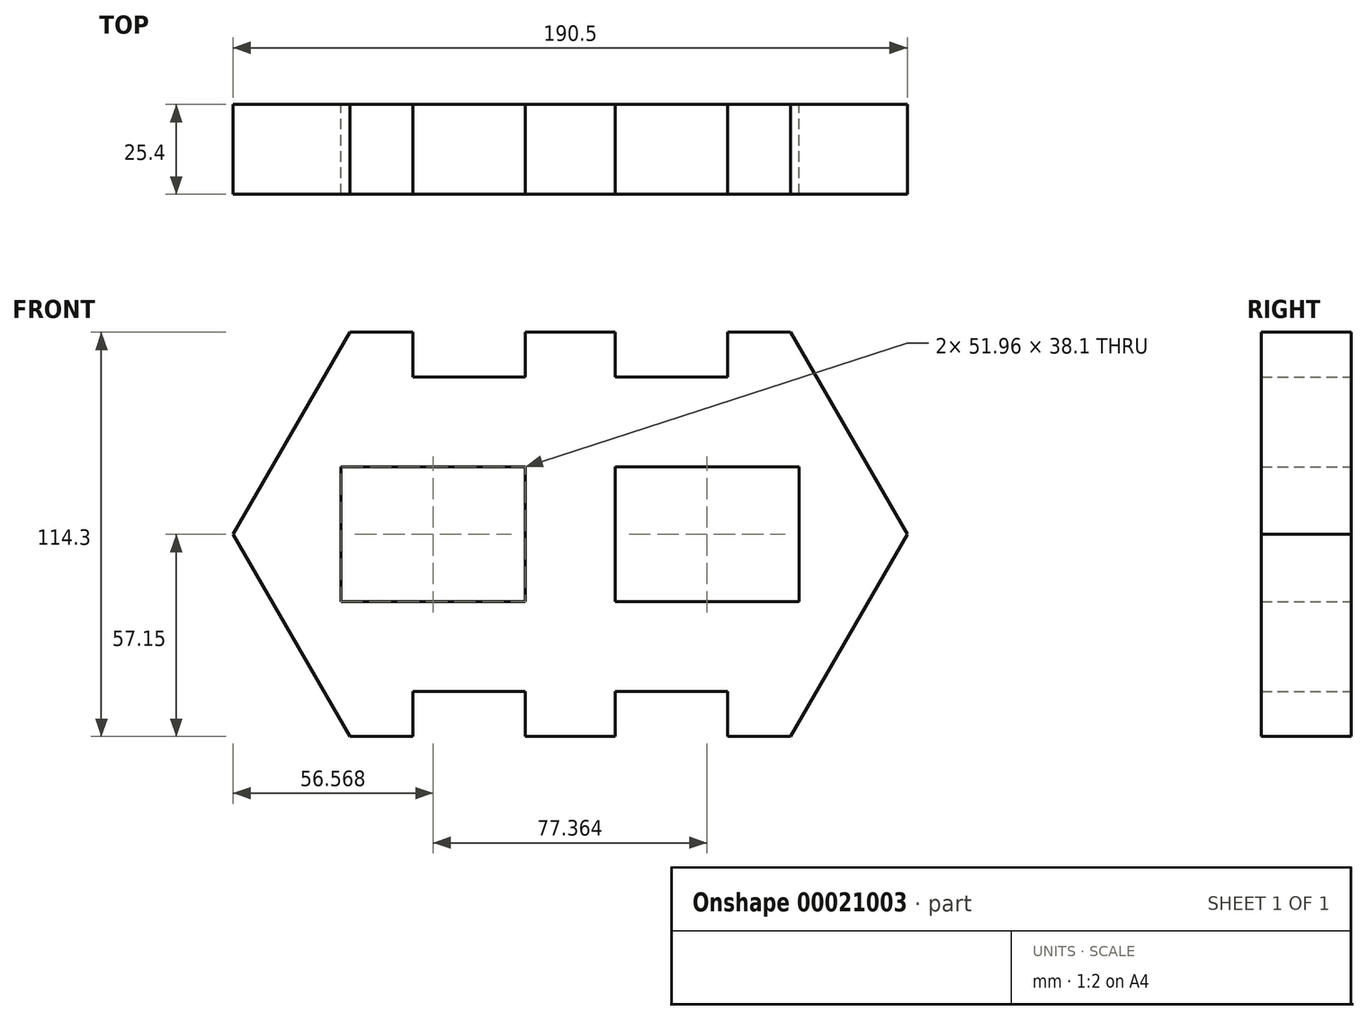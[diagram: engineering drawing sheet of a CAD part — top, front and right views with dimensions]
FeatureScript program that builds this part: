
annotation { "Feature Type Name" : "Feature", "Feature Type Description" : "" }
export const myFeature = defineFeature(function(context is Context, id is Id, definition is map)
    precondition{}
    {
        {
            var Q0;
            Q0=qCreatedBy(makeId("Front.planeOp"),FACE);
            var sketch = newSketch(context, id + "F0", { "sketchPlane" : qUnion([Q0])});
            skLineSegment(sketch, "E0.rect.bottom", {"start": v(-62.25, 57.15) * mm, "end": v(-44.45, 57.15) * mm});
            skLineSegment(sketch, "E0.rect.top", {"start": v(-62.25, -57.15) * mm, "end": v(-44.45, -57.15) * mm});
            skPoint(sketch, "E0.rect.middle", {"position": v(0, 0) * mm});
            skLineSegment(sketch, "E1.rect.bottom", {"start": v(-12.7, 57.15) * mm, "end": v(12.7, 57.15) * mm});
            skLineSegment(sketch, "E1.rect.top", {"start": v(-12.7, -57.15) * mm, "end": v(12.7, -57.15) * mm});
            skLineSegment(sketch, "E1.rect.left", {"start": v(-12.7, 57.15) * mm, "end": v(-12.7, 44.45) * mm});
            skLineSegment(sketch, "E1.rect.right", {"start": v(12.7, 57.15) * mm, "end": v(12.7, 44.45) * mm});
            skPoint(sketch, "E2", {"position": v(12.7, 44.45) * mm});
            skPoint(sketch, "E3", {"position": v(44.45, 57.15) * mm});
            skLineSegment(sketch, "E4", {"start": v(44.45, 57.15) * mm, "end": v(44.45, 44.45) * mm});
            skLineSegment(sketch, "E5", {"start": v(12.7, 44.45) * mm, "end": v(44.45, 44.45) * mm});
            skLineSegment(sketch, "E6", {"start": v(44.45, 44.45) * mm, "end": v(44.45, 57.15) * mm});
            skLineSegment(sketch, "E7.trimOffspring", {"start": v(44.45, 57.15) * mm, "end": v(62.25, 57.15) * mm});
            skPoint(sketch, "E8", {"position": v(64.66, 19.05) * mm});
            skLineSegment(sketch, "E9.bottom", {"start": v(64.66, 19.05) * mm, "end": v(12.7, 19.05) * mm});
            skLineSegment(sketch, "E9.top", {"start": v(64.66, -19.05) * mm, "end": v(12.7, -19.05) * mm});
            skLineSegment(sketch, "E10", {"start": v(95.25, 0) * mm, "end": v(62.25, 57.15) * mm});
            skLineSegment(sketch, "E11", {"start": v(95.25, 0) * mm, "end": v(62.25, -57.15) * mm});
            skLineSegment(sketch, "E12.bottom", {"start": v(12.7, -57.15) * mm, "end": v(-12.7, -57.15) * mm});
            skLineSegment(sketch, "E12.left", {"start": v(12.7, -57.15) * mm, "end": v(12.7, -44.45) * mm});
            skLineSegment(sketch, "E12.right", {"start": v(-12.7, -57.15) * mm, "end": v(-12.7, -44.45) * mm});
            skLineSegment(sketch, "E13", {"start": v(12.7, -44.45) * mm, "end": v(44.45, -44.45) * mm});
            skPoint(sketch, "E14.orphan", {"position": v(95.25, -57.15) * mm});
            skLineSegment(sketch, "E15.trimOffspring", {"start": v(44.45, -44.45) * mm, "end": v(44.45, -57.15) * mm});
            skLineSegment(sketch, "E16", {"start": v(44.45, -57.15) * mm, "end": v(62.25, -57.15) * mm});
            skPoint(sketch, "E17.orphan", {"position": v(95.25, 57.15) * mm});
            skLineSegment(sketch, "E18", {"start": v(64.66, 19.05) * mm, "end": v(64.66, -19.05) * mm});
            skLineSegment(sketch, "E19", {"start": v(12.7, 19.05) * mm, "end": v(12.7, -19.05) * mm});
            skPoint(sketch, "E20", {"position": v(12.7, 19.05) * mm});
            skPoint(sketch, "E21", {"position": v(12.7, -19.05) * mm});
            skPoint(sketch, "E22.orphan", {"position": v(0, -19.05) * mm});
            skLineSegment(sketch, "E23", {"start": v(0, 57.15) * mm, "end": v(0, -57.15) * mm});
            skLineSegment(sketch, "E24.MirrorCS", {"start": v(-12.7, 44.45) * mm, "end": v(-44.45, 44.45) * mm});
            skLineSegment(sketch, "E25.MirrorCS", {"start": v(-44.45, 57.15) * mm, "end": v(-44.45, 44.45) * mm});
            skLineSegment(sketch, "E26.MirrorCS", {"start": v(-64.66, 19.05) * mm, "end": v(-12.7, 19.05) * mm});
            skLineSegment(sketch, "E27.MirrorCS", {"start": v(-64.66, -19.05) * mm, "end": v(-12.7, -19.05) * mm});
            skLineSegment(sketch, "E28.MirrorCS", {"start": v(-12.7, 19.05) * mm, "end": v(-12.7, -19.05) * mm});
            skLineSegment(sketch, "E29.MirrorCS", {"start": v(-64.66, 19.05) * mm, "end": v(-64.66, -19.05) * mm});
            skLineSegment(sketch, "E30.MirrorCS", {"start": v(-12.7, -44.45) * mm, "end": v(-44.45, -44.45) * mm});
            skLineSegment(sketch, "E31.MirrorCS", {"start": v(-44.45, -44.45) * mm, "end": v(-44.45, -57.15) * mm});
            skLineSegment(sketch, "E32.MirrorCS", {"start": v(-44.45, -57.15) * mm, "end": v(-62.25, -57.15) * mm});
            skLineSegment(sketch, "E33.MirrorCS", {"start": v(-95.25, 0) * mm, "end": v(-62.25, -57.15) * mm});
            skLineSegment(sketch, "E34.MirrorCS", {"start": v(-95.25, 0) * mm, "end": v(-62.25, 57.15) * mm});
            skPoint(sketch, "E35.orphan", {"position": v(-95.25, 57.15) * mm});
            skPoint(sketch, "E36.MirrorCS.start.orphan", {"position": v(-95.25, 0) * mm});
            skPoint(sketch, "E37.orphan", {"position": v(-95.25, -57.15) * mm});
            skSolve(sketch);
        }
        {
            var Q0;
            Q0 = qSketchRegion(id + "F0", true);
            extrude(context, id + "F1", {"entities" : qUnion([Q0]), "depth" : 25.4 * mm});
        }
    });
